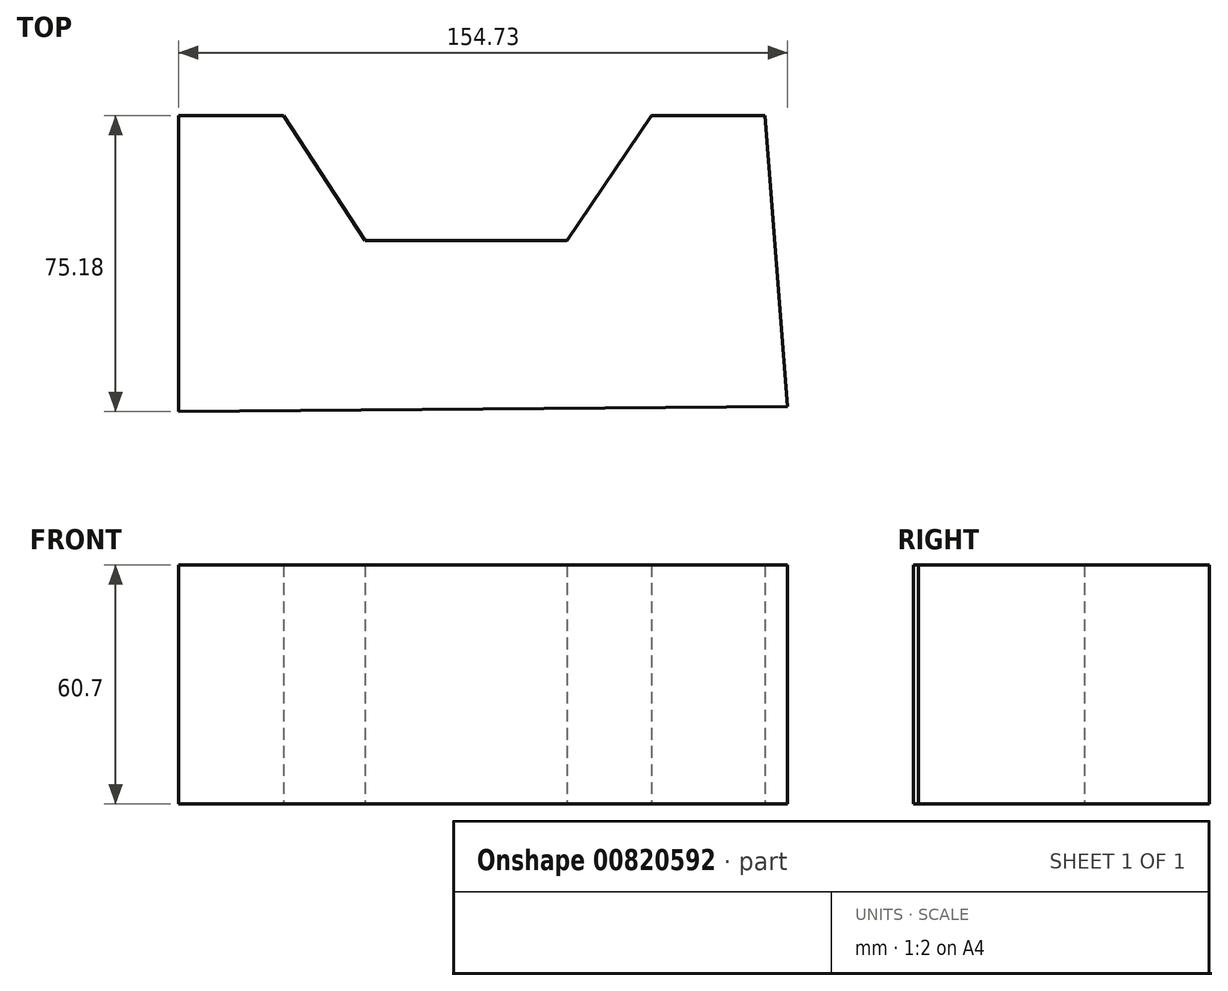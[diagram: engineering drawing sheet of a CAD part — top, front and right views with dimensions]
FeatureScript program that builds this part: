
annotation { "Feature Type Name" : "Feature", "Feature Type Description" : "" }
export const myFeature = defineFeature(function(context is Context, id is Id, definition is map)
    precondition{}
    {
        {
            var Q0;
            Q0=qCreatedBy(makeId("Top.planeOp"),FACE);
            var sketch = newSketch(context, id + "F0", { "sketchPlane" : qUnion([Q0])});
            skLineSegment(sketch, "E0", {"start": v(-131.77, -85.59) * mm, "end": v(-131.77, -10.4) * mm});
            skLineSegment(sketch, "E1", {"start": v(-131.77, -10.4) * mm, "end": v(-105.13, -10.4) * mm});
            skLineSegment(sketch, "E2", {"start": v(-105.13, -10.4) * mm, "end": v(-84.47, -42.2) * mm});
            skLineSegment(sketch, "E3", {"start": v(-84.47, -42.2) * mm, "end": v(-33.1, -42.2) * mm});
            skLineSegment(sketch, "E4", {"start": v(-33.1, -42.2) * mm, "end": v(-11.66, -10.4) * mm});
            skLineSegment(sketch, "E5", {"start": v(-11.66, -10.4) * mm, "end": v(17.17, -10.4) * mm});
            skLineSegment(sketch, "E6", {"start": v(17.17, -10.4) * mm, "end": v(22.96, -84.38) * mm});
            skLineSegment(sketch, "E7", {"start": v(22.96, -84.38) * mm, "end": v(-131.77, -85.59) * mm});
            skSolve(sketch);
        }
        {
            var Q0;
            Q0=makeQuery(id+"F0.imprint","IMPRINT",FACE,{"disambiguationData":[TD([[makeQuery(id+"F0.imprint","IMPRINT",EDGE,{"derivedFrom":sQuery(id+"F0.wireOp",EDGE,"E0")}),-1.0]])]});
            extrude(context, id + "F1", {"entities" : qUnion([Q0]), "depth" : 60.7 * mm, "offsetDistance" : 25 * mm});
        }
    });
